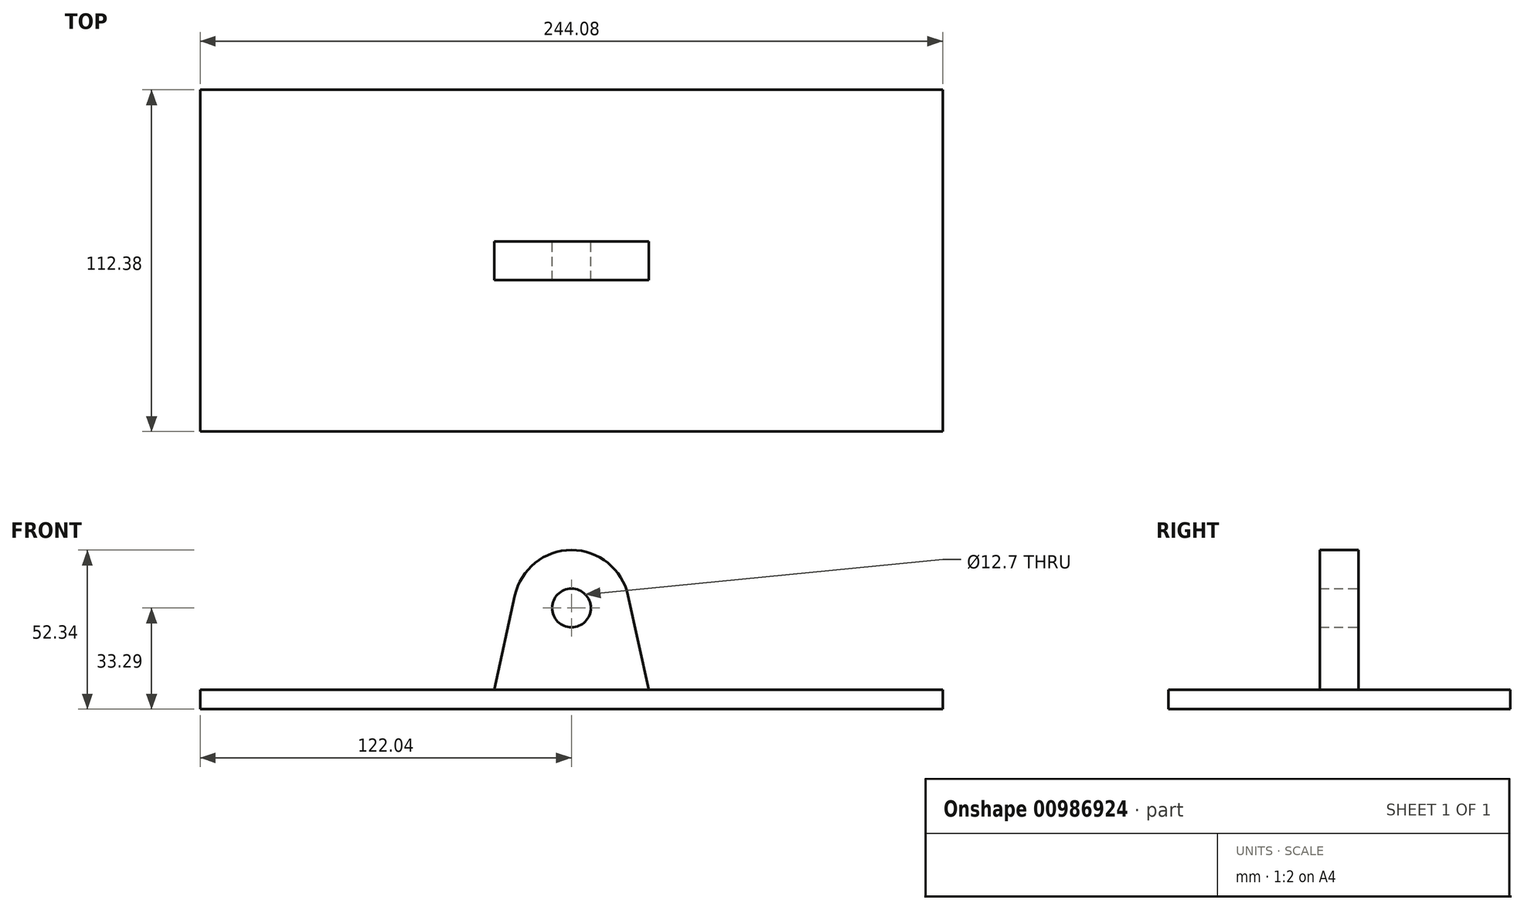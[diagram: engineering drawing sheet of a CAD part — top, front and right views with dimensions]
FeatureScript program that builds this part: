
annotation { "Feature Type Name" : "Feature", "Feature Type Description" : "" }
export const myFeature = defineFeature(function(context is Context, id is Id, definition is map)
    precondition{}
    {
        {
            var Q0;
            Q0=qCreatedBy(makeId("Front.planeOp"),FACE);
            var sketch = newSketch(context, id + "F0", { "sketchPlane" : qUnion([Q0])});
            skArc(sketch, "E0", {"start": v(18.6, 4.07) * mm, "mid": v(0, 19.05) * mm, "end": v(-18.6, 4.07) * mm});
            skCircle(sketch, "E1", {"center": v(0, 0) * mm, "radius": 6.35 * mm});
            skLineSegment(sketch, "E2", {"start": v(18.6, 4.07) * mm, "end": v(25.4, -26.94) * mm});
            skLineSegment(sketch, "E3", {"start": v(25.4, -26.94) * mm, "end": v(-25.4, -26.94) * mm});
            skLineSegment(sketch, "E4", {"start": v(-25.4, -26.94) * mm, "end": v(-18.6, 4.07) * mm});
            skSolve(sketch);
        }
        {
            var Q0;
            Q0 = qSketchRegion(id + "F0", true);
            extrude(context, id + "F1", {"entities" : qUnion([Q0]), "endBound" : BoundingType.SYMMETRIC, "depth" : 12.7 * mm, "offsetDistance" : 25.4 * mm});
        }
        {
            var Q0;
            Q0=makeQuery(id+"F1.opExtrude","SWEPT_FACE",FACE,{"disambiguationData":[OSD([sQuery(id+"F0.wireOp",EDGE,"E3")])]});
            var sketch = newSketch(context, id + "F2", { "sketchPlane" : qUnion([Q0])});
            skLineSegment(sketch, "E5.bottom", {"start": v(-122.04, 56.2) * mm, "end": v(122.04, 56.2) * mm});
            skLineSegment(sketch, "E5.top", {"start": v(-122.04, -56.2) * mm, "end": v(122.04, -56.2) * mm});
            skLineSegment(sketch, "E5.left", {"start": v(-122.04, 56.2) * mm, "end": v(-122.04, -56.2) * mm});
            skLineSegment(sketch, "E5.right", {"start": v(122.04, 56.2) * mm, "end": v(122.04, -56.2) * mm});
            skPoint(sketch, "E5.middle", {"position": v(0, 0) * mm});
            skSolve(sketch);
        }
        {
            var Q0;
            Q0 = qSketchRegion(id + "F2", true);
            extrude(context, id + "F3", {"entities" : qUnion([Q0]), "operationType" : NewBodyOperationType.ADD, "depth" : 6.35 * mm, "offsetDistance" : 25.4 * mm});
        }
    });
